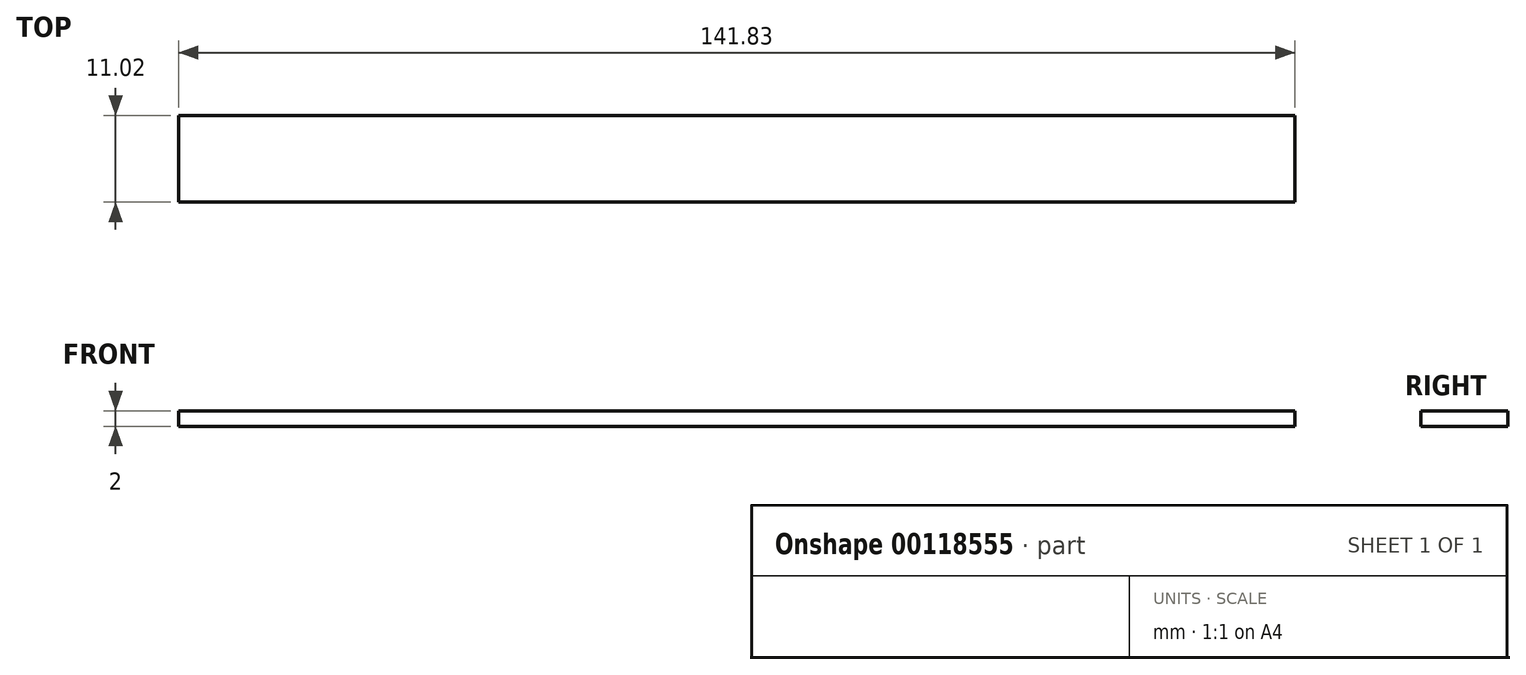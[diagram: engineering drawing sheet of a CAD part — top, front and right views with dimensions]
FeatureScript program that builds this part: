
annotation { "Feature Type Name" : "Feature", "Feature Type Description" : "" }
export const myFeature = defineFeature(function(context is Context, id is Id, definition is map)
    precondition{}
    {
        {
            var Q0;
            Q0=qCreatedBy(makeId("Top.planeOp"),FACE);
            var sketch = newSketch(context, id + "F0", { "sketchPlane" : qUnion([Q0])});
            skLineSegment(sketch, "E0.bottom", {"start": v(-73.96, 14.94) * mm, "end": v(67.87, 14.94) * mm});
            skLineSegment(sketch, "E0.top", {"start": v(-73.96, 3.92) * mm, "end": v(67.87, 3.92) * mm});
            skLineSegment(sketch, "E0.left", {"start": v(-73.96, 14.94) * mm, "end": v(-73.96, 3.92) * mm});
            skLineSegment(sketch, "E0.right", {"start": v(67.87, 14.94) * mm, "end": v(67.87, 3.92) * mm});
            skSolve(sketch);
        }
        {
            var Q0;
            Q0 = qSketchRegion(id + "F0", true);
            extrude(context, id + "F1", {"entities" : qUnion([Q0]), "depth" : 2 * mm});
        }
    });
